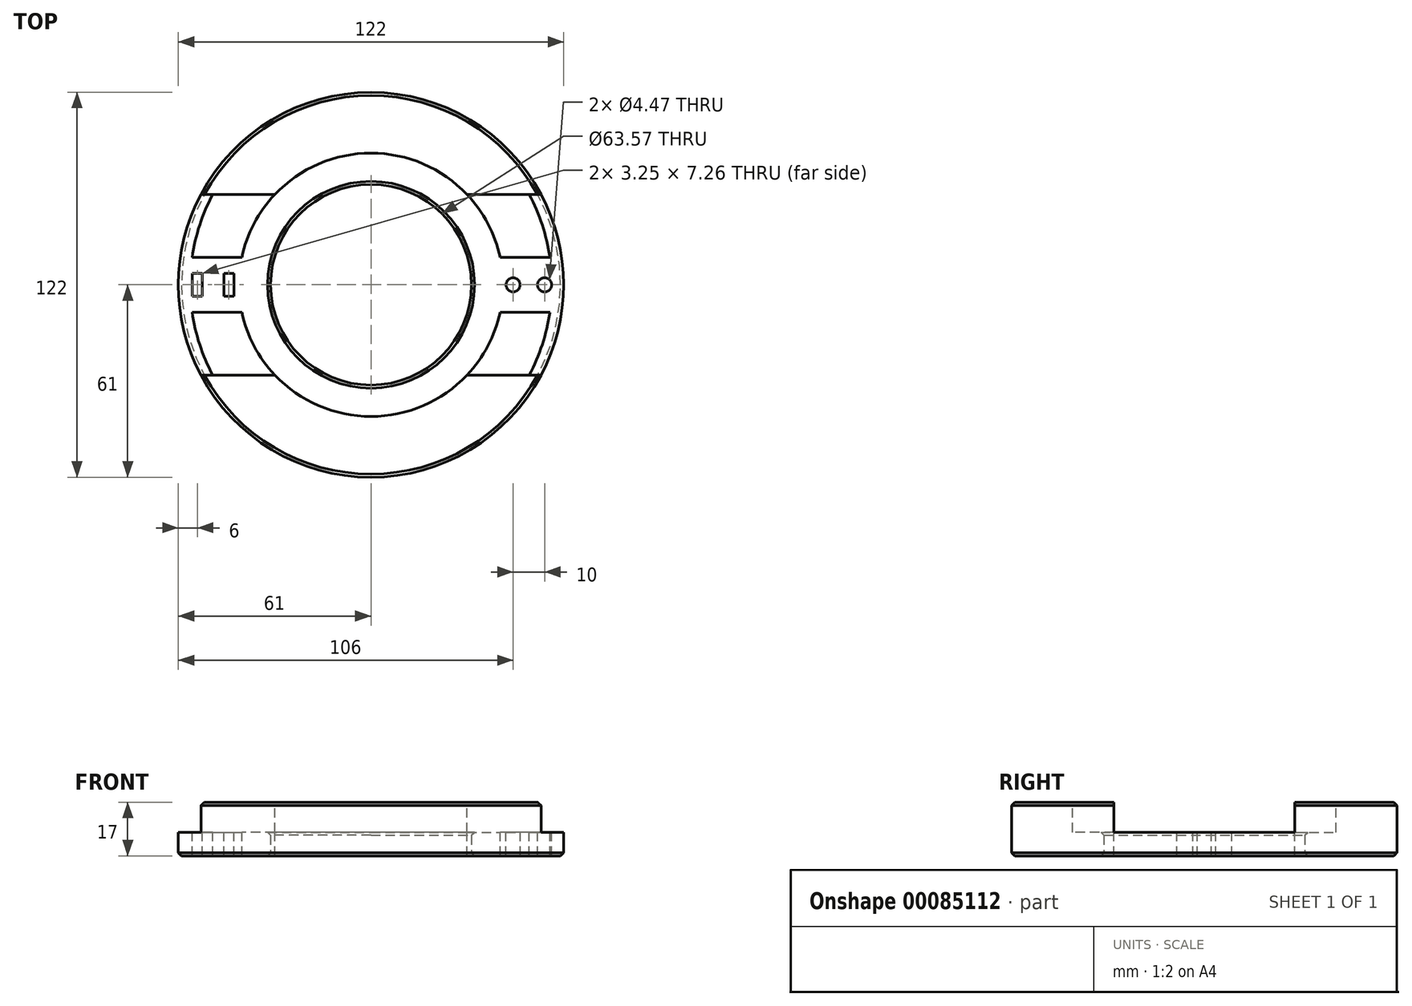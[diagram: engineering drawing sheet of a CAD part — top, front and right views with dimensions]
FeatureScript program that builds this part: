
annotation { "Feature Type Name" : "Feature", "Feature Type Description" : "" }
export const myFeature = defineFeature(function(context is Context, id is Id, definition is map)
    precondition{}
    {
        {
            var Q0;
            Q0=qCreatedBy(makeId("Top.planeOp"),FACE);
            var sketch = newSketch(context, id + "F0", { "sketchPlane" : qUnion([Q0])});
            skCircle(sketch, "E0", {"center": v(0, 0) * mm, "radius": 61 * mm});
            skCircle(sketch, "E1", {"center": v(45, 0) * mm, "radius": 2.24 * mm});
            skCircle(sketch, "E2", {"center": v(55, 0) * mm, "radius": 2.24 * mm});
            skCircle(sketch, "E3", {"center": v(0, 0) * mm, "radius": 53.5 * mm, "construction": true});
            skLineSegment(sketch, "E4", {"start": v(0, 0) * mm, "end": v(-37.83, 37.83) * mm, "construction": true});
            skLineSegment(sketch, "E5", {"start": v(0, 0) * mm, "end": v(-37.83, -37.83) * mm, "construction": true});
            skLineSegment(sketch, "E6.MirrorCS", {"start": v(0, 0) * mm, "end": v(37.83, 37.83) * mm, "construction": true});
            skLineSegment(sketch, "E7.MirrorCS", {"start": v(0, 0) * mm, "end": v(37.83, -37.83) * mm, "construction": true});
            skLineSegment(sketch, "E8", {"start": v(-29, 29) * mm, "end": v(-11.31, 46.67) * mm, "construction": true});
            skLineSegment(sketch, "E9", {"start": v(-29, -29) * mm, "end": v(-11.31, -46.67) * mm, "construction": true});
            skLineSegment(sketch, "E10.bottom", {"start": v(-43.37, 3.63) * mm, "end": v(-46.63, 3.63) * mm});
            skLineSegment(sketch, "E10.top", {"start": v(-43.37, -3.63) * mm, "end": v(-46.63, -3.63) * mm});
            skLineSegment(sketch, "E10.left", {"start": v(-43.37, 3.63) * mm, "end": v(-43.37, -3.63) * mm});
            skLineSegment(sketch, "E10.right", {"start": v(-46.63, 3.63) * mm, "end": v(-46.63, -3.63) * mm});
            skPoint(sketch, "E10.middle", {"position": v(-45, 0) * mm});
            skLineSegment(sketch, "E11.bottom", {"start": v(-53.37, 3.63) * mm, "end": v(-56.63, 3.63) * mm});
            skLineSegment(sketch, "E11.top", {"start": v(-53.37, -3.63) * mm, "end": v(-56.63, -3.63) * mm});
            skLineSegment(sketch, "E11.left", {"start": v(-53.37, 3.63) * mm, "end": v(-53.37, -3.63) * mm});
            skLineSegment(sketch, "E11.right", {"start": v(-56.63, 3.63) * mm, "end": v(-56.63, -3.63) * mm});
            skPoint(sketch, "E11.middle", {"position": v(-55, 0) * mm});
            skSolve(sketch);
        }
        {
            var Q0;
            Q0 = qSketchRegion(id + "F0", true);
            extrude(context, id + "F1", {"entities" : qUnion([Q0]), "depth" : 12 * mm});
        }
        {
            var Q0;
            Q0=makeQuery(id+"F1.opExtrude","CAP_FACE",FACE,{"disambiguationData":[OSD([sQuery(id+"F0.wireOp",EDGE,"E0"),sQuery(id+"F0.wireOp",EDGE,"KwKUaJBB-yk9v-5oBY-24K5-hFvCkIKiBtvL"),sQuery(id+"F0.wireOp",EDGE,"E1"),sQuery(id+"F0.wireOp",EDGE,"E2"),sQuery(id+"F0.wireOp",EDGE,"E10.bottom"),sQuery(id+"F0.wireOp",EDGE,"E10.top"),sQuery(id+"F0.wireOp",EDGE,"E10.left"),sQuery(id+"F0.wireOp",EDGE,"E10.right"),sQuery(id+"F0.wireOp",EDGE,"E11.bottom"),sQuery(id+"F0.wireOp",EDGE,"E11.top"),sQuery(id+"F0.wireOp",EDGE,"E11.left"),sQuery(id+"F0.wireOp",EDGE,"E11.right")])],"isStart":false});
            var sketch = newSketch(context, id + "F2", { "sketchPlane" : qUnion([Q0])});
            skCircle(sketch, "E12", {"center": v(0, 0) * mm, "radius": 31.78 * mm});
            skCircle(sketch, "E13.0", {"center": v(0, 0) * mm, "radius": 41.78 * mm});
            skSolve(sketch);
        }
        {
            var Q0;
            Q0 = qSketchRegion(id + "F2", true);
            extrude(context, id + "F3", {"entities" : qUnion([Q0]), "operationType" : NewBodyOperationType.ADD, "oppositeDirection" : true, "depth" : 2.5 * mm});
        }
        {
            var Q0;
            Q0=makeQuery(id+"F1.opExtrude","CAP_FACE",FACE,{"disambiguationData":[OSD([sQuery(id+"F0.wireOp",EDGE,"E0"),sQuery(id+"F0.wireOp",EDGE,"KwKUaJBB-yk9v-5oBY-24K5-hFvCkIKiBtvL"),sQuery(id+"F0.wireOp",EDGE,"E1"),sQuery(id+"F0.wireOp",EDGE,"E2"),sQuery(id+"F0.wireOp",EDGE,"E10.bottom"),sQuery(id+"F0.wireOp",EDGE,"E10.top"),sQuery(id+"F0.wireOp",EDGE,"E10.left"),sQuery(id+"F0.wireOp",EDGE,"E10.right"),sQuery(id+"F0.wireOp",EDGE,"E11.bottom"),sQuery(id+"F0.wireOp",EDGE,"E11.top"),sQuery(id+"F0.wireOp",EDGE,"E11.left"),sQuery(id+"F0.wireOp",EDGE,"E11.right")])],"isStart":true});
            var sketch = newSketch(context, id + "F4", { "sketchPlane" : qUnion([Q0])});
            skLineSegment(sketch, "E14", {"start": v(-53.52, 8.63) * mm, "end": v(-44.98, 8.63) * mm});
            skPoint(sketch, "E15", {"position": v(-41.51, 8.63) * mm});
            skLineSegment(sketch, "E16", {"start": v(-48.13, 28.63) * mm, "end": v(-33.2, 28.63) * mm});
            skPoint(sketch, "E17", {"position": v(-23.18, 28.63) * mm});
            skPoint(sketch, "E18", {"position": v(-56.63, 8.63) * mm});
            skPoint(sketch, "E19", {"position": v(-60.39, 8.63) * mm});
            skPoint(sketch, "E20", {"position": v(-53.86, 28.63) * mm});
            skArc(sketch, "E21", {"start": v(-31.61, 24.2) * mm, "mid": v(-37.94, 17.73) * mm, "end": v(-42.73, 10.05) * mm});
            skArc(sketch, "E22", {"start": v(-50.38, 27.23) * mm, "mid": v(-53.58, 19.62) * mm, "end": v(-55.95, 11.72) * mm});
            skPoint(sketch, "E23", {"position": v(-53.27, 20.48) * mm});
            skPoint(sketch, "E24", {"position": v(-40.73, 13.71) * mm});
            skPoint(sketch, "E25", {"position": v(-38.87, 13.71) * mm});
            skPoint(sketch, "E26", {"position": v(-57.46, 20.48) * mm});
            skArc(sketch, "E27.filletArc", {"start": v(-55.95, 11.72) * mm, "mid": v(-55.48, 9.59) * mm, "end": v(-53.52, 8.63) * mm});
            skPoint(sketch, "E28.visualSharp", {"position": v(-43.37, 8.63) * mm});
            skArc(sketch, "E28.filletArc", {"start": v(-44.98, 8.63) * mm, "mid": v(-43.65, 9.02) * mm, "end": v(-42.73, 10.05) * mm});
            skPoint(sketch, "E29.visualSharp", {"position": v(-49.67, 28.63) * mm});
            skArc(sketch, "E29.filletArc", {"start": v(-48.13, 28.63) * mm, "mid": v(-49.46, 28.25) * mm, "end": v(-50.38, 27.23) * mm});
            skPoint(sketch, "E30.visualSharp", {"position": v(-25.04, 28.63) * mm});
            skArc(sketch, "E30.filletArc", {"start": v(-31.61, 24.2) * mm, "mid": v(-30.85, 26.98) * mm, "end": v(-33.2, 28.63) * mm});
            skLineSegment(sketch, "E31.MirrorCS", {"start": v(-53.52, -8.63) * mm, "end": v(-44.98, -8.63) * mm});
            skArc(sketch, "E32.MirrorCS", {"start": v(-44.98, -8.63) * mm, "mid": v(-43.65, -9.02) * mm, "end": v(-42.73, -10.05) * mm});
            skArc(sketch, "E33.MirrorCS", {"start": v(-31.61, -24.2) * mm, "mid": v(-37.94, -17.73) * mm, "end": v(-42.73, -10.05) * mm});
            skArc(sketch, "E34.MirrorCS", {"start": v(-55.95, -11.72) * mm, "mid": v(-55.48, -9.59) * mm, "end": v(-53.52, -8.63) * mm});
            skArc(sketch, "E35.MirrorCS", {"start": v(-50.38, -27.23) * mm, "mid": v(-53.58, -19.62) * mm, "end": v(-55.95, -11.72) * mm});
            skArc(sketch, "E36.MirrorCS", {"start": v(-48.13, -28.63) * mm, "mid": v(-49.46, -28.25) * mm, "end": v(-50.38, -27.23) * mm});
            skLineSegment(sketch, "E37.MirrorCS", {"start": v(-48.13, -28.63) * mm, "end": v(-33.2, -28.63) * mm});
            skArc(sketch, "E38.MirrorCS", {"start": v(-31.61, -24.2) * mm, "mid": v(-30.85, -26.98) * mm, "end": v(-33.2, -28.63) * mm});
            skLineSegment(sketch, "E39.MirrorCS", {"start": v(53.52, 8.63) * mm, "end": v(44.98, 8.63) * mm});
            skArc(sketch, "E40.MirrorCS", {"start": v(44.98, 8.63) * mm, "mid": v(43.65, 9.02) * mm, "end": v(42.73, 10.05) * mm});
            skArc(sketch, "E41.MirrorCS", {"start": v(31.61, 24.2) * mm, "mid": v(37.94, 17.73) * mm, "end": v(42.73, 10.05) * mm});
            skArc(sketch, "E42.MirrorCS", {"start": v(55.95, 11.72) * mm, "mid": v(55.48, 9.59) * mm, "end": v(53.52, 8.63) * mm});
            skArc(sketch, "E43.MirrorCS", {"start": v(50.38, 27.23) * mm, "mid": v(53.58, 19.62) * mm, "end": v(55.95, 11.72) * mm});
            skLineSegment(sketch, "E44.MirrorCS", {"start": v(48.13, 28.63) * mm, "end": v(33.2, 28.63) * mm});
            skArc(sketch, "E45.MirrorCS", {"start": v(31.61, 24.2) * mm, "mid": v(30.85, 26.98) * mm, "end": v(33.2, 28.63) * mm});
            skArc(sketch, "E46.MirrorCS", {"start": v(48.13, 28.63) * mm, "mid": v(49.46, 28.25) * mm, "end": v(50.38, 27.23) * mm});
            skArc(sketch, "E47.MirrorCS", {"start": v(50.38, -27.23) * mm, "mid": v(53.58, -19.62) * mm, "end": v(55.95, -11.72) * mm});
            skLineSegment(sketch, "E48.MirrorCS", {"start": v(48.13, -28.63) * mm, "end": v(33.2, -28.63) * mm});
            skArc(sketch, "E49.MirrorCS", {"start": v(31.61, -24.2) * mm, "mid": v(37.94, -17.73) * mm, "end": v(42.73, -10.05) * mm});
            skLineSegment(sketch, "E50.MirrorCS", {"start": v(53.52, -8.63) * mm, "end": v(44.98, -8.63) * mm});
            skArc(sketch, "E51.MirrorCS", {"start": v(44.98, -8.63) * mm, "mid": v(43.65, -9.02) * mm, "end": v(42.73, -10.05) * mm});
            skArc(sketch, "E52.MirrorCS", {"start": v(55.95, -11.72) * mm, "mid": v(55.48, -9.59) * mm, "end": v(53.52, -8.63) * mm});
            skArc(sketch, "E53.MirrorCS", {"start": v(48.13, -28.63) * mm, "mid": v(49.46, -28.25) * mm, "end": v(50.38, -27.23) * mm});
            skArc(sketch, "E54.MirrorCS", {"start": v(31.61, -24.2) * mm, "mid": v(30.85, -26.98) * mm, "end": v(33.2, -28.63) * mm});
            skSolve(sketch);
        }
        {
            var Q0;
            Q0=makeQuery(id+"F3.boolean.opBoolean","MERGE",FACE,{"derivedFrom":[makeQuery(id+"F1.opExtrude","CAP_FACE",FACE,{"disambiguationData":[OSD([sQuery(id+"F0.wireOp",EDGE,"E0"),sQuery(id+"F0.wireOp",EDGE,"KwKUaJBB-yk9v-5oBY-24K5-hFvCkIKiBtvL"),sQuery(id+"F0.wireOp",EDGE,"E1"),sQuery(id+"F0.wireOp",EDGE,"E2"),sQuery(id+"F0.wireOp",EDGE,"E10.bottom"),sQuery(id+"F0.wireOp",EDGE,"E10.top"),sQuery(id+"F0.wireOp",EDGE,"E10.left"),sQuery(id+"F0.wireOp",EDGE,"E10.right"),sQuery(id+"F0.wireOp",EDGE,"E11.bottom"),sQuery(id+"F0.wireOp",EDGE,"E11.top"),sQuery(id+"F0.wireOp",EDGE,"E11.left"),sQuery(id+"F0.wireOp",EDGE,"E11.right")])],"isStart":false}),makeQuery(id+"F3.opExtrude","CAP_FACE",FACE,{"disambiguationData":[OSD([sQuery(id+"F2.wireOp",EDGE,"E12"),sQuery(id+"F2.wireOp",EDGE,"E13.0")])],"isStart":true})]});
            var sketch = newSketch(context, id + "F5", { "sketchPlane" : qUnion([Q0])});
            skCircle(sketch, "E55.0", {"center": v(0, 0) * mm, "radius": 41.78 * mm});
            skCircle(sketch, "E56.0", {"center": v(0, 0) * mm, "radius": 61 * mm});
            skSolve(sketch);
        }
        {
            var Q0;
            Q0=makeQuery(id+"F1.opExtrude","CAP_FACE",FACE,{"disambiguationData":[OSD([sQuery(id+"F0.wireOp",EDGE,"E0"),sQuery(id+"F0.wireOp",EDGE,"E1"),sQuery(id+"F0.wireOp",EDGE,"E2"),sQuery(id+"F0.wireOp",EDGE,"E10.bottom"),sQuery(id+"F0.wireOp",EDGE,"E10.top"),sQuery(id+"F0.wireOp",EDGE,"E10.left"),sQuery(id+"F0.wireOp",EDGE,"E10.right"),sQuery(id+"F0.wireOp",EDGE,"E11.bottom"),sQuery(id+"F0.wireOp",EDGE,"E11.top"),sQuery(id+"F0.wireOp",EDGE,"E11.left"),sQuery(id+"F0.wireOp",EDGE,"E11.right")])],"isStart":true});
            var sketch = newSketch(context, id + "F6", { "sketchPlane" : qUnion([Q0])});
            skPoint(sketch, "E57.middle", {"position": v(0, 0) * mm});
            skLineSegment(sketch, "E58.bottom", {"start": v(-64.2, 20) * mm, "end": v(64.2, 20) * mm});
            skLineSegment(sketch, "E58.top", {"start": v(-64.2, -20) * mm, "end": v(64.2, -20) * mm});
            skLineSegment(sketch, "E58.left", {"start": v(-64.2, 20) * mm, "end": v(-64.2, -20) * mm});
            skLineSegment(sketch, "E58.right", {"start": v(64.2, 20) * mm, "end": v(64.2, -20) * mm});
            skSolve(sketch);
        }
        {
            var Q0;
            Q0 = qSketchRegion(id + "F6", true);
            var Q1;
            Q1=makeQuery(id+"F3.opExtrude","CAP_FACE",FACE,{"disambiguationData":[OSD([sQuery(id+"F2.wireOp",EDGE,"E12"),sQuery(id+"F2.wireOp",EDGE,"E13.0")])],"isStart":false});
            extrude(context, id + "F7", {"entities" : qUnion([Q0]), "operationType" : NewBodyOperationType.REMOVE, "oppositeDirection" : true, "endBoundEntityFace" : qUnion([Q1]), "depth" : 9.5 * mm});
        }
        {
            var Q0;
            Q0=qCreatedBy(makeId("Top.planeOp"),FACE);
            cPlane(context, id + "F8", {"entities" : qUnion([Q0]), "cplaneType" : CPlaneType.OFFSET, "offset" : 150 * mm, "oppositeDirection" : true, "width" : 150 * mm, "height" : 150 * mm});
        }
        {
            var Q0;
            Q0=qCreatedBy(id+"F8.planeOp",FACE);
            var sketch = newSketch(context, id + "F9", { "sketchPlane" : qUnion([Q0])});
            skPoint(sketch, "E59", {"position": v(0, 0) * mm});
            skSolve(sketch);
        }
        {
            var Q0;
            Q0=sQuery(id+"F9.wireOp",VERTEX,"E59");
            var Q1;
            Q1=makeQuery(id+"F1.opExtrude","SWEPT_BODY",BODY,{"disambiguationData":[OSD([sQuery(id+"F0.wireOp",EDGE,"E0"),sQuery(id+"F0.wireOp",EDGE,"E1"),sQuery(id+"F0.wireOp",EDGE,"E2"),sQuery(id+"F0.wireOp",EDGE,"E10.bottom"),sQuery(id+"F0.wireOp",EDGE,"E10.top"),sQuery(id+"F0.wireOp",EDGE,"E10.left"),sQuery(id+"F0.wireOp",EDGE,"E10.right"),sQuery(id+"F0.wireOp",EDGE,"E11.bottom"),sQuery(id+"F0.wireOp",EDGE,"E11.top"),sQuery(id+"F0.wireOp",EDGE,"E11.left"),sQuery(id+"F0.wireOp",EDGE,"E11.right")])]});
            hole(context, id + "F10", {"style" : HoleStyle.SIMPLE, "endStyle" : HoleEndStyle.THROUGH, "oppositeDirection" : true, "holeDiameter" : 83.5 * mm, "locations" : qUnion([Q0]), "scope" : qUnion([Q1]), "isTappedThrough" : true});
        }
        {
            var Q0;
            Q0=makeQuery(id+"F5.imprint","IMPRINT",FACE,{"disambiguationData":[TD([[makeQuery(id+"F5.imprint","IMPRINT",EDGE,{"derivedFrom":sQuery(id+"F5.wireOp",EDGE,"E55.0")}),-1.0]])]});
            var sketch = newSketch(context, id + "F11", { "sketchPlane" : qUnion([Q0])});
            skCircle(sketch, "E60.0", {"center": v(0, 0) * mm, "radius": 41.78 * mm});
            skCircle(sketch, "E61", {"center": v(0, 0) * mm, "radius": 31.78 * mm});
            skSolve(sketch);
        }
        {
            var Q0;
            Q0 = qSketchRegion(id + "F11", true);
            var Q1;
            {var subQ0=sQuery(id+"F6.wireOp",EDGE,"E58.top");var subQ1=sQuery(id+"F6.wireOp",EDGE,"E58.bottom");Q1=makeQuery(id+"F10.hole-0.boolean.opBoolean","SPLIT",FACE,{"disambiguationData":[TD([makeQuery(id+"F1.opExtrude","SWEPT_FACE",FACE,{"disambiguationData":[OSD([sQuery(id+"F0.wireOp",EDGE,"E10.bottom")])]})])],"derivedFrom":makeQuery(id+"F7.boolean.opBoolean","COPY",FACE,{"derivedFrom":makeQuery(id+"F7.opExtrude","CAP_FACE",FACE,{"disambiguationData":[OSD([subQ1,subQ0,sQuery(id+"F6.wireOp",EDGE,"E58.left"),sQuery(id+"F6.wireOp",EDGE,"E58.right")])],"isStart":false})})});}
            extrude(context, id + "F12", {"entities" : qUnion([Q0]), "operationType" : NewBodyOperationType.ADD, "endBound" : BoundingType.UP_TO_SURFACE, "oppositeDirection" : true, "endBoundEntityFace" : qUnion([Q1]), "depth" : 25 * mm});
        }
        {
            var Q0;
            {var subQ2=sQuery(id+"F6.wireOp",EDGE,"E58.bottom");var subQ4=sQuery(id+"F6.wireOp",EDGE,"E58.top");var subQ6=makeQuery(id+"F7.boolean.opBoolean","COPY",FACE,{"derivedFrom":makeQuery(id+"F7.opExtrude","CAP_FACE",FACE,{"disambiguationData":[OSD([subQ2,subQ4,sQuery(id+"F6.wireOp",EDGE,"E58.left"),sQuery(id+"F6.wireOp",EDGE,"E58.right")])],"isStart":false})});Q0=makeQuery(id+"F12.boolean.opBoolean","MERGE",FACE,{"derivedFrom":[makeQuery(id+"F10.hole-0.boolean.opBoolean","SPLIT",FACE,{"disambiguationData":[TD([makeQuery(id+"F1.opExtrude","SWEPT_FACE",FACE,{"disambiguationData":[OSD([sQuery(id+"F0.wireOp",EDGE,"E1")])]})])],"derivedFrom":subQ6}),makeQuery(id+"F10.hole-0.boolean.opBoolean","SPLIT",FACE,{"disambiguationData":[TD([makeQuery(id+"F1.opExtrude","SWEPT_FACE",FACE,{"disambiguationData":[OSD([sQuery(id+"F0.wireOp",EDGE,"E10.bottom")])]})])],"derivedFrom":subQ6}),makeQuery(id+"F12.opExtrude","CAP_FACE",FACE,{"disambiguationData":[OSD([sQuery(id+"F11.wireOp",EDGE,"E60.0"),sQuery(id+"F11.wireOp",EDGE,"E61")])],"isStart":false})]});}
            var sketch = newSketch(context, id + "F13", { "sketchPlane" : qUnion([Q0])});
            skLineSegment(sketch, "E62", {"start": v(-56.63, 8.68) * mm, "end": v(-40.87, 8.68) * mm});
            skLineSegment(sketch, "E63", {"start": v(-50.1, 28.63) * mm, "end": v(-30.43, 28.63) * mm});
            skCircle(sketch, "E64.0", {"center": v(0, 0) * mm, "radius": 41.78 * mm, "construction": true});
            skPoint(sketch, "E65", {"position": v(-30.43, 28.63) * mm});
            skPoint(sketch, "E66", {"position": v(-40.87, 8.68) * mm});
            skPoint(sketch, "E67", {"position": v(-60.38, 8.68) * mm});
            skPoint(sketch, "E68", {"position": v(-53.86, 28.63) * mm});
            skArc(sketch, "E69", {"start": v(-50.1, 28.63) * mm, "mid": v(-54.23, 18.94) * mm, "end": v(-56.63, 8.68) * mm});
            skArc(sketch, "E70", {"start": v(-30.43, 28.63) * mm, "mid": v(-37.02, 19.37) * mm, "end": v(-40.87, 8.68) * mm});
            skPoint(sketch, "E71", {"position": v(-37.02, 19.37) * mm});
            skPoint(sketch, "E72", {"position": v(-54.23, 18.94) * mm});
            skPoint(sketch, "E73", {"position": v(-57.99, 18.94) * mm});
            skArc(sketch, "E74.MirrorCS", {"start": v(30.43, 28.63) * mm, "mid": v(37.02, 19.37) * mm, "end": v(40.87, 8.68) * mm});
            skLineSegment(sketch, "E75.MirrorCS", {"start": v(50.1, 28.63) * mm, "end": v(30.43, 28.63) * mm});
            skArc(sketch, "E76.MirrorCS", {"start": v(50.1, 28.63) * mm, "mid": v(54.23, 18.94) * mm, "end": v(56.63, 8.68) * mm});
            skLineSegment(sketch, "E77.MirrorCS", {"start": v(56.63, 8.68) * mm, "end": v(40.87, 8.68) * mm});
            skLineSegment(sketch, "E78.MirrorCS", {"start": v(-56.63, -8.68) * mm, "end": v(-40.87, -8.68) * mm});
            skArc(sketch, "E79.MirrorCS", {"start": v(-50.1, -28.63) * mm, "mid": v(-54.23, -18.94) * mm, "end": v(-56.63, -8.68) * mm});
            skLineSegment(sketch, "E80.MirrorCS", {"start": v(-50.1, -28.63) * mm, "end": v(-30.43, -28.63) * mm});
            skArc(sketch, "E81.MirrorCS", {"start": v(-30.43, -28.63) * mm, "mid": v(-37.02, -19.37) * mm, "end": v(-40.87, -8.68) * mm});
            skArc(sketch, "E82.MirrorCS", {"start": v(30.43, -28.63) * mm, "mid": v(37.02, -19.37) * mm, "end": v(40.87, -8.68) * mm});
            skLineSegment(sketch, "E83.MirrorCS", {"start": v(50.1, -28.63) * mm, "end": v(30.43, -28.63) * mm});
            skArc(sketch, "E84.MirrorCS", {"start": v(50.1, -28.63) * mm, "mid": v(54.23, -18.94) * mm, "end": v(56.63, -8.68) * mm});
            skLineSegment(sketch, "E85.MirrorCS", {"start": v(56.63, -8.68) * mm, "end": v(40.87, -8.68) * mm});
            skSolve(sketch);
        }
        {
            var Q0;
            Q0 = qSketchRegion(id + "F13", true);
            extrude(context, id + "F14", {"entities" : qUnion([Q0]), "operationType" : NewBodyOperationType.REMOVE, "endBound" : BoundingType.THROUGH_ALL, "oppositeDirection" : true, "depth" : 25 * mm});
        }
        {
            var Q0;
            {var subQ0=sQuery(id+"F0.wireOp",EDGE,"E0");Q0=makeQuery(id+"F7.boolean.opBoolean","SPLIT",FACE,{"disambiguationData":[TD([makeQuery(id+"F7.opExtrude","SWEPT_FACE",FACE,{"disambiguationData":[OSD([sQuery(id+"F6.wireOp",EDGE,"E58.bottom")])]})])],"derivedFrom":makeQuery(id+"F1.opExtrude","CAP_FACE",FACE,{"disambiguationData":[OSD([subQ0,sQuery(id+"F0.wireOp",EDGE,"E1"),sQuery(id+"F0.wireOp",EDGE,"E2"),sQuery(id+"F0.wireOp",EDGE,"E10.bottom"),sQuery(id+"F0.wireOp",EDGE,"E10.top"),sQuery(id+"F0.wireOp",EDGE,"E10.left"),sQuery(id+"F0.wireOp",EDGE,"E10.right"),sQuery(id+"F0.wireOp",EDGE,"E11.bottom"),sQuery(id+"F0.wireOp",EDGE,"E11.top"),sQuery(id+"F0.wireOp",EDGE,"E11.left"),sQuery(id+"F0.wireOp",EDGE,"E11.right")])],"isStart":true})});}
            var sketch = newSketch(context, id + "F15", { "sketchPlane" : qUnion([Q0])});
            skArc(sketch, "E86.0.0", {"start": v(-53.87, 20) * mm, "mid": v(-52.16, 24.39) * mm, "end": v(-50.1, 28.63) * mm, "construction": true});
            skLineSegment(sketch, "E86.0.1", {"start": v(-50.1, 28.63) * mm, "end": v(-30.43, 28.63) * mm, "construction": true});
            skArc(sketch, "E86.0.2", {"start": v(-30.43, 28.63) * mm, "mid": v(-33.84, 24.52) * mm, "end": v(-36.69, 20) * mm, "construction": true});
            skLineSegment(sketch, "E86.0.3", {"start": v(-36.69, 20) * mm, "end": v(-53.87, 20) * mm, "construction": true});
            skCircle(sketch, "E87.0", {"center": v(0, 0) * mm, "radius": 31.78 * mm, "construction": true});
            skLineSegment(sketch, "E88.bottom", {"start": v(-63.4, 28.63) * mm, "end": v(63.4, 28.63) * mm});
            skLineSegment(sketch, "E88.top", {"start": v(-63.4, -28.63) * mm, "end": v(63.4, -28.63) * mm});
            skLineSegment(sketch, "E88.left", {"start": v(-63.4, 28.63) * mm, "end": v(-63.4, -28.63) * mm});
            skLineSegment(sketch, "E88.right", {"start": v(63.4, 28.63) * mm, "end": v(63.4, -28.63) * mm});
            skSolve(sketch);
        }
        {
            var Q0;
            Q0 = qSketchRegion(id + "F15", true);
            var Q1;
            {var subQ2=sQuery(id+"F6.wireOp",EDGE,"E58.bottom");var subQ4=sQuery(id+"F6.wireOp",EDGE,"E58.top");var subQ6=makeQuery(id+"F7.boolean.opBoolean","COPY",FACE,{"derivedFrom":makeQuery(id+"F7.opExtrude","CAP_FACE",FACE,{"disambiguationData":[OSD([subQ2,subQ4,sQuery(id+"F6.wireOp",EDGE,"E58.left"),sQuery(id+"F6.wireOp",EDGE,"E58.right")])],"isStart":false})});Q1=makeQuery(id+"F12.boolean.opBoolean","MERGE",FACE,{"derivedFrom":[makeQuery(id+"F10.hole-0.boolean.opBoolean","SPLIT",FACE,{"disambiguationData":[TD([makeQuery(id+"F1.opExtrude","SWEPT_FACE",FACE,{"disambiguationData":[OSD([sQuery(id+"F0.wireOp",EDGE,"E1")])]})])],"derivedFrom":subQ6}),makeQuery(id+"F10.hole-0.boolean.opBoolean","SPLIT",FACE,{"disambiguationData":[TD([makeQuery(id+"F1.opExtrude","SWEPT_FACE",FACE,{"disambiguationData":[OSD([sQuery(id+"F0.wireOp",EDGE,"E10.bottom")])]})])],"derivedFrom":subQ6}),makeQuery(id+"F12.opExtrude","CAP_FACE",FACE,{"disambiguationData":[OSD([sQuery(id+"F11.wireOp",EDGE,"E60.0"),sQuery(id+"F11.wireOp",EDGE,"E61")])],"isStart":false})]});}
            extrude(context, id + "F16", {"entities" : qUnion([Q0]), "operationType" : NewBodyOperationType.REMOVE, "endBound" : BoundingType.UP_TO_SURFACE, "oppositeDirection" : true, "endBoundEntityFace" : qUnion([Q1]), "depth" : 25 * mm});
        }
        {
            var Q0;
            Q0=qCreatedBy(makeId("Top.planeOp"),FACE);
            var sketch = newSketch(context, id + "F17", { "sketchPlane" : qUnion([Q0])});
            skCircle(sketch, "E89.0", {"center": v(0, 0) * mm, "radius": 31.78 * mm, "construction": true});
            skLineSegment(sketch, "E90", {"start": v(0, 0) * mm, "end": v(-77.13, 0) * mm, "construction": true});
            skSolve(sketch);
        }
        {
            var Q0;
            Q0=makeQuery(id+"F1.opExtrude","SWEPT_BODY",BODY,{"disambiguationData":[OSD([sQuery(id+"F0.wireOp",EDGE,"E0"),sQuery(id+"F0.wireOp",EDGE,"E1"),sQuery(id+"F0.wireOp",EDGE,"E2"),sQuery(id+"F0.wireOp",EDGE,"E10.bottom"),sQuery(id+"F0.wireOp",EDGE,"E10.top"),sQuery(id+"F0.wireOp",EDGE,"E10.left"),sQuery(id+"F0.wireOp",EDGE,"E10.right"),sQuery(id+"F0.wireOp",EDGE,"E11.bottom"),sQuery(id+"F0.wireOp",EDGE,"E11.top"),sQuery(id+"F0.wireOp",EDGE,"E11.left"),sQuery(id+"F0.wireOp",EDGE,"E11.right")])]});
            var Q1;
            Q1=sQuery(id+"F17.wireOp",EDGE,"E90");
            transform(context, id + "F18", {"entities" : qUnion([Q0]), "transformType" : TransformType.ROTATION, "transformAxis" : qUnion([Q1]), "angle" : 180 * degree, "makeCopy" : false});
        }
        {
            var Q0;
            Q0=makeQuery(id+"F12.boolean.opBoolean","MERGE",FACE,{"derivedFrom":[makeQuery(id+"F1.opExtrude","CAP_FACE",FACE,{"disambiguationData":[OSD([sQuery(id+"F0.wireOp",EDGE,"E0"),sQuery(id+"F0.wireOp",EDGE,"E1"),sQuery(id+"F0.wireOp",EDGE,"E2"),sQuery(id+"F0.wireOp",EDGE,"E10.bottom"),sQuery(id+"F0.wireOp",EDGE,"E10.top"),sQuery(id+"F0.wireOp",EDGE,"E10.left"),sQuery(id+"F0.wireOp",EDGE,"E10.right"),sQuery(id+"F0.wireOp",EDGE,"E11.bottom"),sQuery(id+"F0.wireOp",EDGE,"E11.top"),sQuery(id+"F0.wireOp",EDGE,"E11.left"),sQuery(id+"F0.wireOp",EDGE,"E11.right")])],"isStart":false}),makeQuery(id+"F12.opExtrude","CAP_FACE",FACE,{"disambiguationData":[OSD([sQuery(id+"F11.wireOp",EDGE,"E60.0"),sQuery(id+"F11.wireOp",EDGE,"E61")])],"isStart":true})]});
            extrude(context, id + "F19", {"entities" : qUnion([Q0]), "operationType" : NewBodyOperationType.ADD, "depth" : 5 * mm, "offsetDistance" : 25 * mm});
        }
        {
            var Q0;
            {var subQ0=sQuery(id+"F0.wireOp",EDGE,"E0");Q0=makeQuery(id+"F10.hole-0.boolean.opBoolean","INTERSECT",EDGE,{"derivedFrom":[makeQuery(id+"F7.boolean.opBoolean","SPLIT",FACE,{"disambiguationData":[TD([makeQuery(id+"F7.opExtrude","SWEPT_FACE",FACE,{"disambiguationData":[OSD([sQuery(id+"F6.wireOp",EDGE,"E58.top")])]})])],"derivedFrom":makeQuery(id+"F1.opExtrude","CAP_FACE",FACE,{"disambiguationData":[OSD([subQ0,sQuery(id+"F0.wireOp",EDGE,"E1"),sQuery(id+"F0.wireOp",EDGE,"E2"),sQuery(id+"F0.wireOp",EDGE,"E10.bottom"),sQuery(id+"F0.wireOp",EDGE,"E10.top"),sQuery(id+"F0.wireOp",EDGE,"E10.left"),sQuery(id+"F0.wireOp",EDGE,"E10.right"),sQuery(id+"F0.wireOp",EDGE,"E11.bottom"),sQuery(id+"F0.wireOp",EDGE,"E11.top"),sQuery(id+"F0.wireOp",EDGE,"E11.left"),sQuery(id+"F0.wireOp",EDGE,"E11.right")])],"isStart":true})}),makeQuery(id+"F10.hole-0.opRevolve","SWEPT_FACE",FACE,{"disambiguationData":[OSD([sQuery(id+"F10.hole-0.sketch.wireOp",EDGE,"core_line_2")])]})]});}
            var Q1;
            {var subQ0=sQuery(id+"F0.wireOp",EDGE,"E0");Q1=makeQuery(id+"F10.hole-0.boolean.opBoolean","INTERSECT",EDGE,{"derivedFrom":[makeQuery(id+"F7.boolean.opBoolean","SPLIT",FACE,{"disambiguationData":[TD([makeQuery(id+"F7.opExtrude","SWEPT_FACE",FACE,{"disambiguationData":[OSD([sQuery(id+"F6.wireOp",EDGE,"E58.bottom")])]})])],"derivedFrom":makeQuery(id+"F1.opExtrude","CAP_FACE",FACE,{"disambiguationData":[OSD([subQ0,sQuery(id+"F0.wireOp",EDGE,"E1"),sQuery(id+"F0.wireOp",EDGE,"E2"),sQuery(id+"F0.wireOp",EDGE,"E10.bottom"),sQuery(id+"F0.wireOp",EDGE,"E10.top"),sQuery(id+"F0.wireOp",EDGE,"E10.left"),sQuery(id+"F0.wireOp",EDGE,"E10.right"),sQuery(id+"F0.wireOp",EDGE,"E11.bottom"),sQuery(id+"F0.wireOp",EDGE,"E11.top"),sQuery(id+"F0.wireOp",EDGE,"E11.left"),sQuery(id+"F0.wireOp",EDGE,"E11.right")])],"isStart":true})}),makeQuery(id+"F10.hole-0.opRevolve","SWEPT_FACE",FACE,{"disambiguationData":[OSD([sQuery(id+"F10.hole-0.sketch.wireOp",EDGE,"core_line_2")])]})]});}
            var Q2;
            Q2=makeQuery(id+"F12.opExtrude","CAP_EDGE",EDGE,{"disambiguationData":[OSD([sQuery(id+"F11.wireOp",EDGE,"E61")])],"isStart":false});
            var Q3;
            Q3=makeQuery(id+"F16.boolean.opBoolean","COPY",EDGE,{"disambiguationData":[OD(1.0)],"derivedFrom":makeQuery(id+"F16.opExtrude","CAP_EDGE",EDGE,{"disambiguationData":[OSD([sQuery(id+"F15.wireOp",EDGE,"E88.top")])],"isStart":true})});
            var Q4;
            {var subQ0=sQuery(id+"F0.wireOp",EDGE,"E0");Q4=makeQuery(id+"F7.boolean.opBoolean","SPLIT",EDGE,{"disambiguationData":[TD([makeQuery(id+"F7.opExtrude","SWEPT_FACE",FACE,{"disambiguationData":[OSD([sQuery(id+"F6.wireOp",EDGE,"E58.top")])]})])],"derivedFrom":makeQuery(id+"F1.opExtrude","CAP_EDGE",EDGE,{"disambiguationData":[OSD([subQ0])],"isStart":true})});}
            var Q5;
            Q5=makeQuery(id+"F16.boolean.opBoolean","COPY",EDGE,{"disambiguationData":[OD(0.0)],"derivedFrom":makeQuery(id+"F16.opExtrude","CAP_EDGE",EDGE,{"disambiguationData":[OSD([sQuery(id+"F15.wireOp",EDGE,"E88.top")])],"isStart":true})});
            var Q6;
            Q6=makeQuery(id+"F16.boolean.opBoolean","COPY",EDGE,{"disambiguationData":[OD(0.0)],"derivedFrom":makeQuery(id+"F16.opExtrude","CAP_EDGE",EDGE,{"disambiguationData":[OSD([sQuery(id+"F15.wireOp",EDGE,"E88.bottom")])],"isStart":true})});
            var Q7;
            {var subQ0=sQuery(id+"F0.wireOp",EDGE,"E0");Q7=makeQuery(id+"F7.boolean.opBoolean","SPLIT",EDGE,{"disambiguationData":[TD([makeQuery(id+"F7.opExtrude","SWEPT_FACE",FACE,{"disambiguationData":[OSD([sQuery(id+"F6.wireOp",EDGE,"E58.bottom")])]})])],"derivedFrom":makeQuery(id+"F1.opExtrude","CAP_EDGE",EDGE,{"disambiguationData":[OSD([subQ0])],"isStart":true})});}
            var Q8;
            Q8=makeQuery(id+"F16.boolean.opBoolean","COPY",EDGE,{"disambiguationData":[OD(1.0)],"derivedFrom":makeQuery(id+"F16.opExtrude","CAP_EDGE",EDGE,{"disambiguationData":[OSD([sQuery(id+"F15.wireOp",EDGE,"E88.bottom")])],"isStart":true})});
            var Q9;
            Q9=makeQuery(id+"F19.opExtrude","CAP_EDGE",EDGE,{"disambiguationData":[OSD([sQuery(id+"F11.wireOp",EDGE,"E61")])],"isStart":false});
            var Q10;
            Q10=makeQuery(id+"F19.opExtrude","CAP_EDGE",EDGE,{"disambiguationData":[OSD([sQuery(id+"F0.wireOp",EDGE,"E0")])],"isStart":false});
            var Q11;
            Q11=makeQuery(id+"F16.boolean.opBoolean","INTERSECT",EDGE,{"disambiguationData":[OD(1.0)],"derivedFrom":[makeQuery(id+"F1.opExtrude","SWEPT_FACE",FACE,{"disambiguationData":[OSD([sQuery(id+"F0.wireOp",EDGE,"E0")])]}),makeQuery(id+"F16.opExtrude","CAP_FACE",FACE,{"disambiguationData":[OSD([sQuery(id+"F6.wireOp",EDGE,"E58.bottom"),sQuery(id+"F6.wireOp",EDGE,"E58.top"),sQuery(id+"F6.wireOp",EDGE,"E58.left"),sQuery(id+"F6.wireOp",EDGE,"E58.right"),sQuery(id+"F11.wireOp",EDGE,"E60.0"),sQuery(id+"F11.wireOp",EDGE,"E61")])],"isStart":false})]});
            var Q12;
            Q12=makeQuery(id+"F16.boolean.opBoolean","INTERSECT",EDGE,{"disambiguationData":[OD(0.0)],"derivedFrom":[makeQuery(id+"F1.opExtrude","SWEPT_FACE",FACE,{"disambiguationData":[OSD([sQuery(id+"F0.wireOp",EDGE,"E0")])]}),makeQuery(id+"F16.opExtrude","CAP_FACE",FACE,{"disambiguationData":[OSD([sQuery(id+"F6.wireOp",EDGE,"E58.bottom"),sQuery(id+"F6.wireOp",EDGE,"E58.top"),sQuery(id+"F6.wireOp",EDGE,"E58.left"),sQuery(id+"F6.wireOp",EDGE,"E58.right"),sQuery(id+"F11.wireOp",EDGE,"E60.0"),sQuery(id+"F11.wireOp",EDGE,"E61")])],"isStart":false})]});
            chamfer(context, id + "F20", {"entities" : qUnion([Q0, Q1, Q2, Q3, Q4, Q5, Q6, Q7, Q8, Q9, Q10, Q11, Q12]), "width" : 1 * mm, "tangentPropagation" : true});
        }
    });
